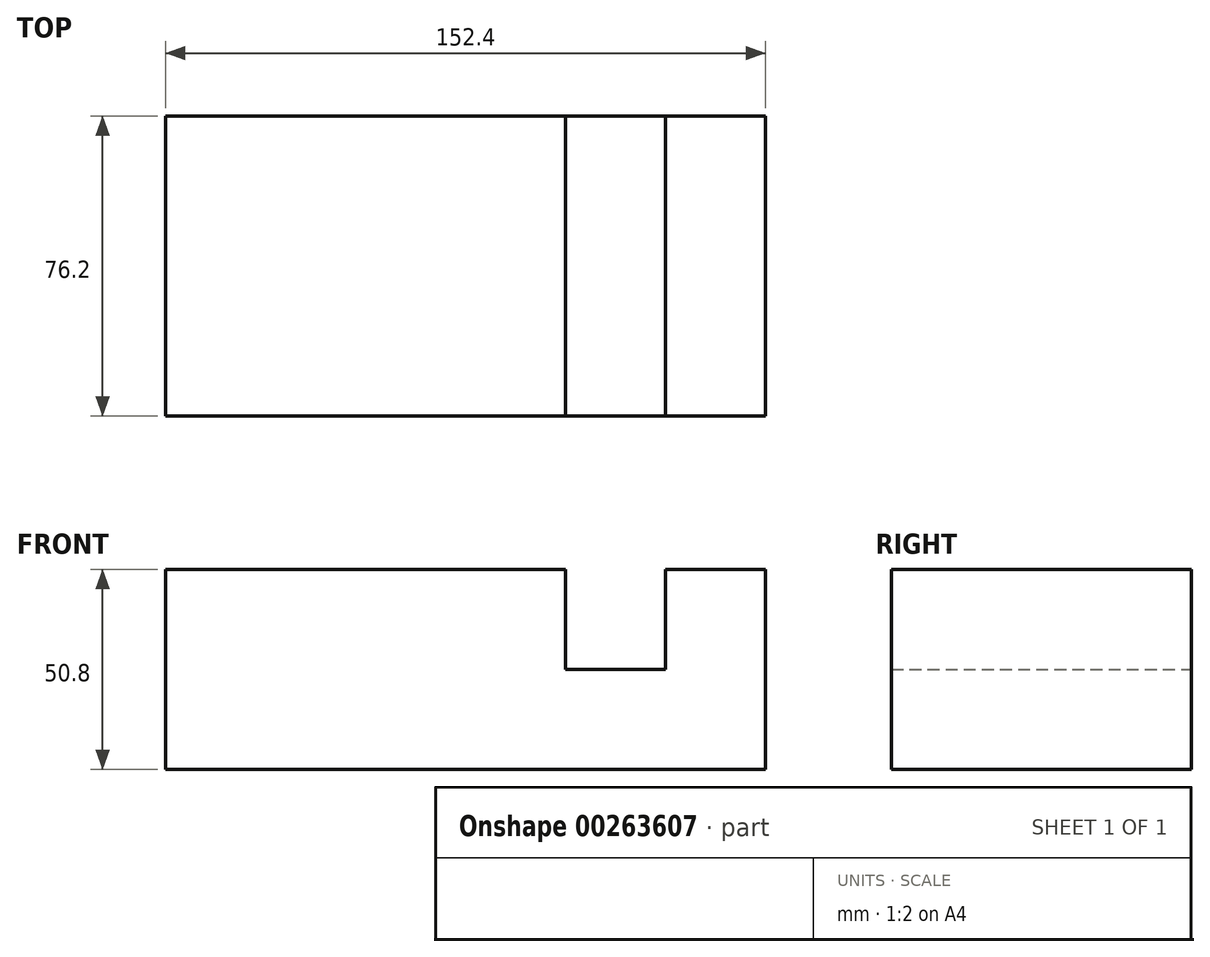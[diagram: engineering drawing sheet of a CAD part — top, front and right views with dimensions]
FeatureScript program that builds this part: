
annotation { "Feature Type Name" : "Feature", "Feature Type Description" : "" }
export const myFeature = defineFeature(function(context is Context, id is Id, definition is map)
    precondition{}
    {
        {
            var Q0;
            Q0=qCreatedBy(makeId("Front.planeOp"),FACE);
            var sketch = newSketch(context, id + "F0", { "sketchPlane" : qUnion([Q0])});
            skLineSegment(sketch, "E0", {"start": v(-76.68, 0) * mm, "end": v(-76.68, -50.8) * mm});
            skLineSegment(sketch, "E1", {"start": v(-76.68, -50.8) * mm, "end": v(75.72, -50.8) * mm});
            skLineSegment(sketch, "E2", {"start": v(75.72, -50.8) * mm, "end": v(75.72, 0) * mm});
            skLineSegment(sketch, "E3", {"start": v(75.72, 0) * mm, "end": v(50.32, 0) * mm});
            skLineSegment(sketch, "E4", {"start": v(50.32, 0) * mm, "end": v(50.32, -25.4) * mm});
            skLineSegment(sketch, "E5", {"start": v(50.32, -25.4) * mm, "end": v(24.92, -25.4) * mm});
            skLineSegment(sketch, "E6", {"start": v(24.92, -25.4) * mm, "end": v(24.92, 0) * mm});
            skLineSegment(sketch, "E7", {"start": v(24.92, 0) * mm, "end": v(-76.68, 0) * mm});
            skSolve(sketch);
        }
        {
            var Q0;
            Q0=makeQuery(id+"F0.imprint","IMPRINT",FACE,{"disambiguationData":[TD([[makeQuery(id+"F0.imprint","IMPRINT",EDGE,{"derivedFrom":sQuery(id+"F0.wireOp",EDGE,"E0")}),1.0]])]});
            extrude(context, id + "F1", {"entities" : qUnion([Q0]), "depth" : 76.2 * mm});
        }
    });
